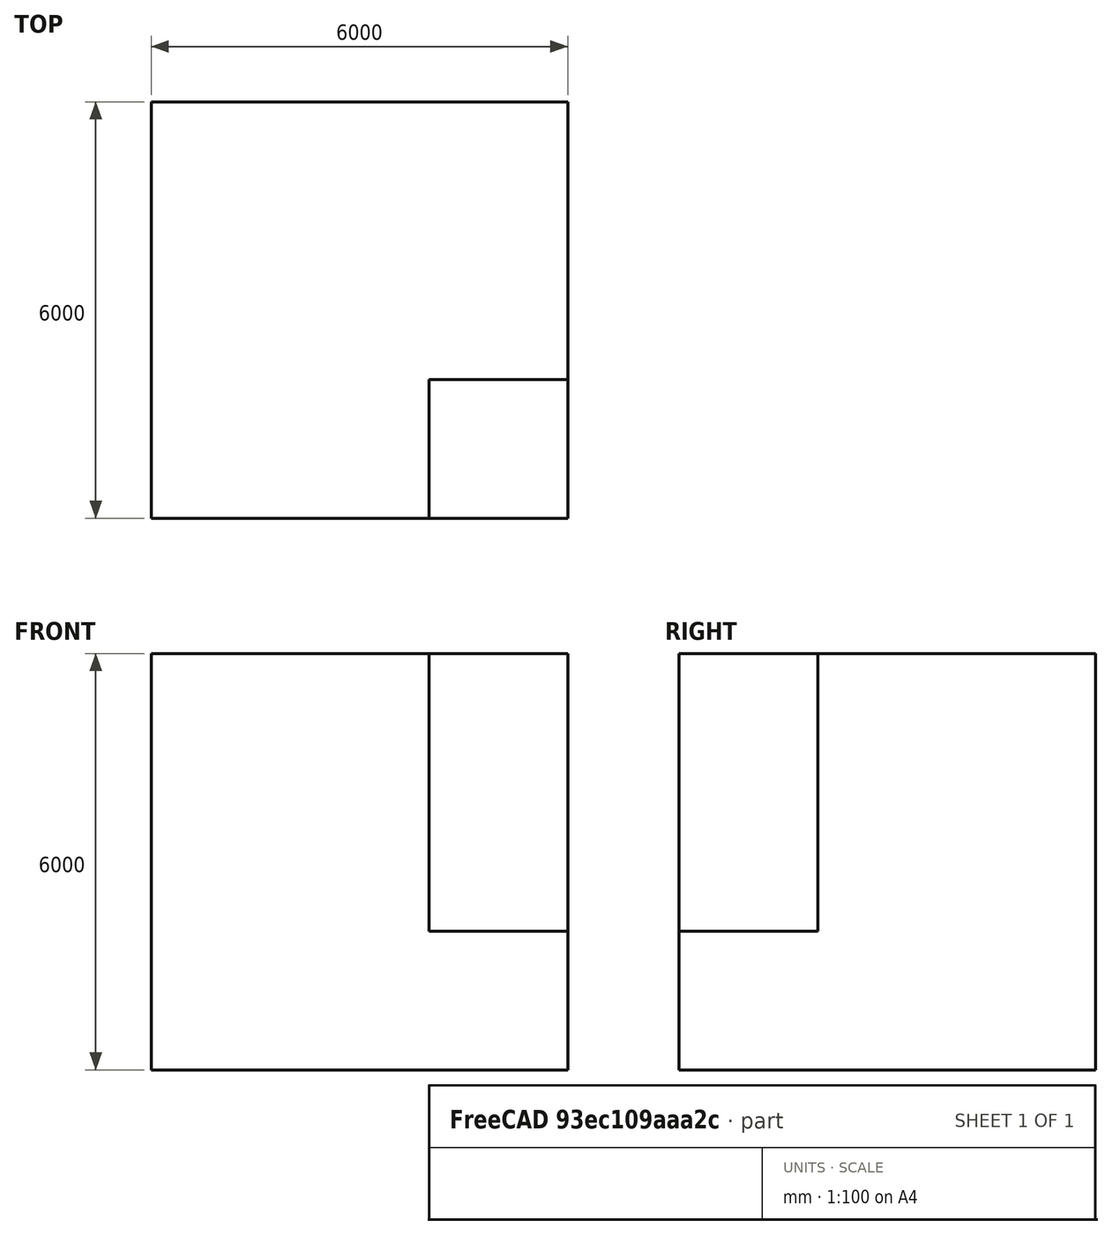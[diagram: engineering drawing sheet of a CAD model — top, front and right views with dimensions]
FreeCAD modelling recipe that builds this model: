
FCSTD DOCUMENT  (FreeCAD 0.21R33771 (Git))
Label: Pit_Example
License: All rights reserved
LicenseURL: http://en.wikipedia.org/wiki/All_rights_reserved
objects: Fem::ConstraintDisplacement×3, Part::Box×2, Part::FeaturePython×1, Fem::FemMeshObjectPython×1, App::MaterialObjectPython×1, Fem::FemSolverObjectPython×1, Fem::FemAnalysis×1
note: 3 computed .brp shape members not serialized (recipe doc carries the construction recipe); baked Part::Feature solids carry a one-line shape summary decoded from their .brp

FEATURE [Part::Box] Box  label="Cube"
  AttacherType = Attacher::AttachEngine3D
  Height = 6000
  Length = 6000
  Width = 6000
FEATURE [Part::Box] Box001  label="Cube001"
  AttacherType = Attacher::AttachEngine3D
  Height = 4000
  Length = 2000
  Placement = pos=(4000,0,2000) rot=(0,0,1;0rad)
  Width = 2000
FEATURE [Part::FeaturePython] XOR  # WARN: FeaturePython — macro-defined, semantics opaque (R4)
  Objects = -> [Box,Box001]
  Tolerance = 0
FEATURE [Fem::FemMeshObjectPython] FEMMeshGmsh  # FEM object (typed FeaturePython)
  Algorithm2D = 0
  Algorithm3D = 0
  CharacteristicLengthMax = 1000
  CharacteristicLengthMin = 1000
  CoherenceMesh = true
  ElementDimension = 0
  ElementOrder = 1
  GeometryTolerance = 1e-06
  GroupsOfNodes = false
  HighOrderOptimize = 0
  MeshSizeFromCurvature = 12
  OptimizeNetgen = false
  OptimizeStd = true
  Part = -> XOR
  RecombinationAlgorithm = 0
  Recombine3DAll = false
  RecombineAll = false
  SecondOrderLinear = false
FEATURE [Fem::ConstraintDisplacement] FemConstraintDisplacement
  NormalDirection = (0,-1,0)
  Normals = (82) [(0,-1,0),(0,-1,0),(0,-1,0),(0,-1,0),(0,-1,0),(0,-1,0),(0,-1,0),(0,-1,0),(0,-1,0),(0,-1,0),(0,-1,0),(0,-1,0),(0,-1,0),(0,-1,0),(0,-1,0),(0,-1,0),+66 more]
  Points = (82) [(0,0,0),(0,0,666.667),(0,0,1333.33),(0,0,2000),(0,0,2666.67),(0,0,3333.33),(0,0,4000),(0,0,4666.67),(0,0,5333.33),(0,0,6000),(666.667,0,0),+71 more]
  References = -> [XOR]
  Scale = 66
  hasXFormula = false
  hasYFormula = false
  hasZFormula = false
  rotxFix = false
  rotxFree = true
  rotyFix = false
  rotyFree = true
  rotzFix = false
  rotzFree = true
  useFlowSurfaceForce = false
  xDisplacement = 0
  xFix = false
  xFree = true
  xRotation = 0
  yDisplacement = 0
  yFix = true
  yFree = false
  yRotation = 0
  zDisplacement = 0
  zFix = false
  zFree = true
  zRotation = 0
FEATURE [Fem::ConstraintDisplacement] FemConstraintDisplacement001
  NormalDirection = (1,0,0)
  Normals = (82) [(1,0,0),(1,0,0),(1,0,0),(1,0,0),(1,0,0),(1,0,0),(1,0,0),(1,0,0),(1,0,0),(1,0,0),(1,0,0),(1,0,0),(1,0,0),(1,0,0),(1,0,0),(1,0,0),(1,0,0),(1,0,0),+64 more]
  Points = (82) [(6000,6000,0),(6000,6000,666.667),(6000,6000,1333.33),(6000,6000,2000),(6000,6000,2666.67),(6000,6000,3333.33),(6000,6000,4000),(6000,6000,4666.67),+74 more]
  References = -> [XOR]
  Scale = 66
  hasXFormula = false
  hasYFormula = false
  hasZFormula = false
  rotxFix = false
  rotxFree = true
  rotyFix = false
  rotyFree = true
  rotzFix = false
  rotzFree = true
  useFlowSurfaceForce = false
  xDisplacement = 0
  xFix = true
  xFree = false
  xRotation = 0
  yDisplacement = 0
  yFix = false
  yFree = true
  yRotation = 0
  zDisplacement = 0
  zFix = false
  zFree = true
  zRotation = 0
FEATURE [Fem::ConstraintDisplacement] FemConstraintDisplacement002
  NormalDirection = (-1,0,0)
  Normals = (300) [(-1,0,0),(-1,0,0),(-1,0,0),(-1,0,0),(-1,0,0),(-1,0,0),(-1,0,0),(-1,0,0),(-1,0,0),(-1,0,0),(-1,0,0),(-1,0,0),(-1,0,0),(-1,0,0),(-1,0,0),(-1,0,0),+284 more]
  Points = (300) [(0,6000,0),(0,6000,666.667),(0,6000,1333.33),(0,6000,2000),(0,6000,2666.67),(0,6000,3333.33),(0,6000,4000),(0,6000,4666.67),(0,6000,5333.33),+291 more]
  References = -> [XOR]
  Scale = 66
  hasXFormula = false
  hasYFormula = false
  hasZFormula = false
  rotxFix = false
  rotxFree = true
  rotyFix = false
  rotyFree = true
  rotzFix = false
  rotzFree = true
  useFlowSurfaceForce = false
  xDisplacement = 0
  xFix = true
  xFree = false
  xRotation = 0
  yDisplacement = 0
  yFix = true
  yFree = false
  yRotation = 0
  zDisplacement = 0
  zFix = true
  zFree = false
  zRotation = 0
FEATURE [App::MaterialObjectPython] SolidMaterial  # material (typed FeaturePython)
  Category = 0
  Material = Density=2000 kg/m^3,Description=Standard steel material for CalculiX sample calculations,Father=Metal,Name=CalculiX-Steel,PoissonRatio=0.3,+4 more (map truncated)
FEATURE [Fem::FemSolverObjectPython] SolverCcxTools  # FEM object (typed FeaturePython)
  AnalysisType = 0
  BeamShellResultOutput3D = false
  BucklingFactors = 1
  EigenmodeHighLimit = 1000000
  EigenmodeLowLimit = 0
  EigenmodesCount = 10
  GeometricalNonlinearity = 0
  IterationsControlParameterCutb = 0.25,0.5,0.75,0.85,,,1.5,
  IterationsControlParameterIter = 4,8,9,200,10,400,,200,,
  IterationsControlParameterTimeUse = false
  IterationsThermoMechMaximum = 2000
  IterationsUserDefinedIncrementations = false
  IterationsUserDefinedTimeStepLength = false
  MaterialNonlinearity = 0
  MatrixSolverType = 0
  SplitInputWriter = false
  ThermoMechSteadyState = true
  TimeEnd = 1
  TimeInitialStep = 0.01
FEATURE [Fem::FemAnalysis] Analysis
  Group = -> [FEMMeshGmsh,FemConstraintDisplacement,FemConstraintDisplacement001,FemConstraintDisplacement002,SolidMaterial,SolverCcxTools]
